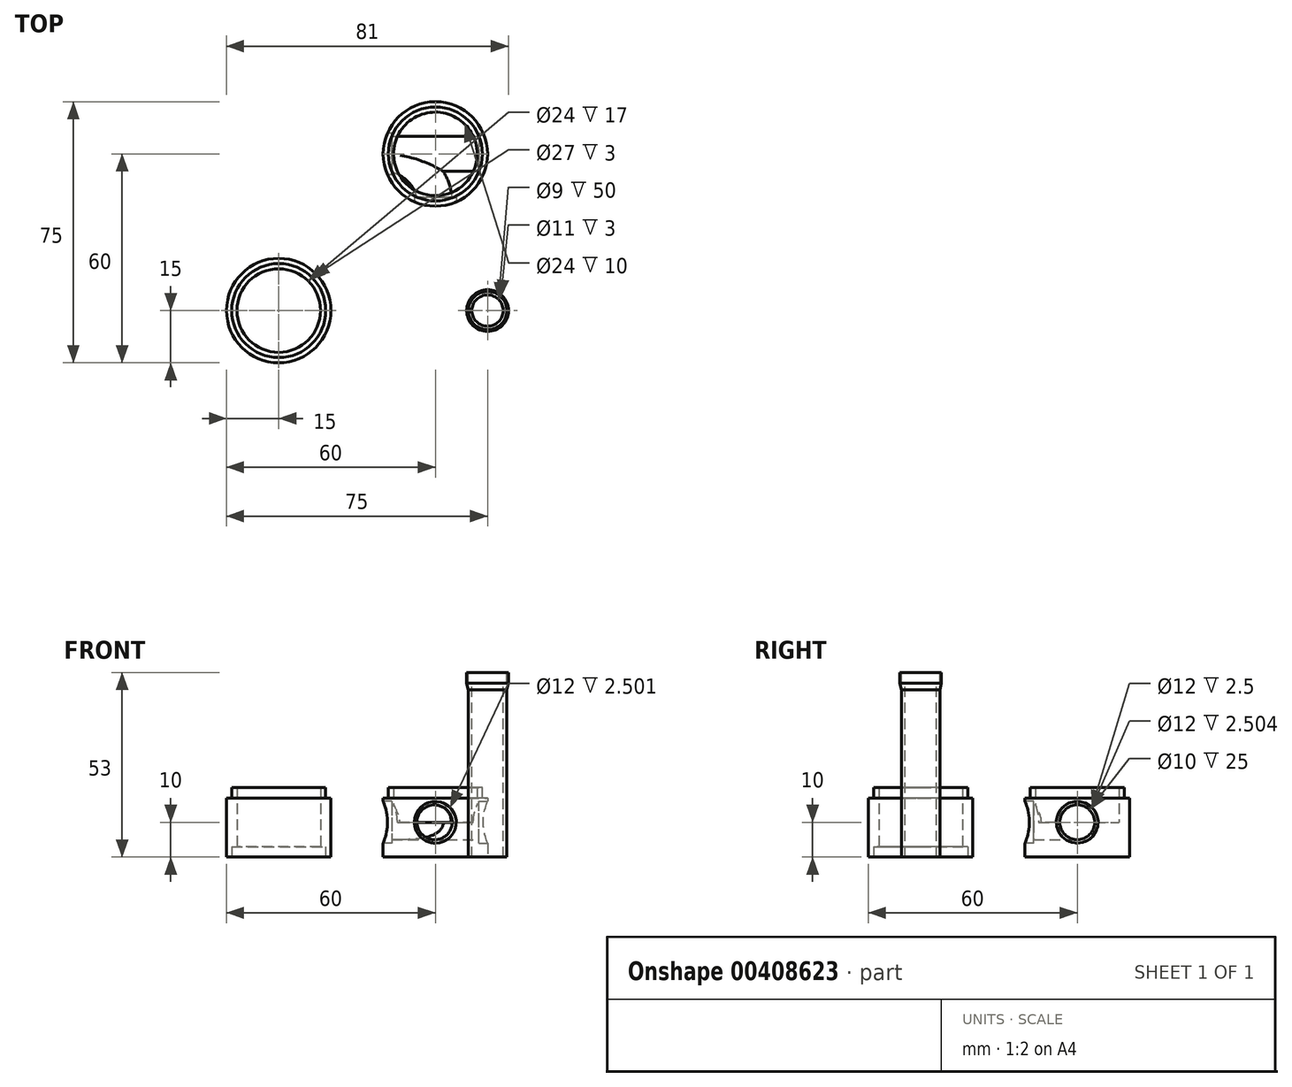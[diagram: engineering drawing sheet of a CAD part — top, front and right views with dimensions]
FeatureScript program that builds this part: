
annotation { "Feature Type Name" : "Feature", "Feature Type Description" : "" }
export const myFeature = defineFeature(function(context is Context, id is Id, definition is map)
    precondition{}
    {
        {
            var Q0;
            Q0=qCreatedBy(makeId("Top.planeOp"),FACE);
            var sketch = newSketch(context, id + "F0", { "sketchPlane" : qUnion([Q0])});
            skLineSegment(sketch, "E0.bottom", {"start": v(0, 0) * mm, "end": v(30, 0) * mm});
            skLineSegment(sketch, "E0.top", {"start": v(0, 30) * mm, "end": v(30, 30) * mm});
            skLineSegment(sketch, "E0.left", {"start": v(0, 0) * mm, "end": v(0, 30) * mm});
            skLineSegment(sketch, "E0.right", {"start": v(30, 0) * mm, "end": v(30, 30) * mm});
            skSolve(sketch);
        }
        {
            var Q0;
            Q0 = qSketchRegion(id + "F0", true);
            extrude(context, id + "F1", {"entities" : qUnion([Q0]), "depth" : 10 * mm});
        }
        {
            var Q0;
            Q0=makeQuery(id+"F1.opExtrude","CAP_FACE",FACE,{"disambiguationData":[OSD([sQuery(id+"F0.wireOp",EDGE,"E0.bottom"),sQuery(id+"F0.wireOp",EDGE,"E0.top"),sQuery(id+"F0.wireOp",EDGE,"E0.left"),sQuery(id+"F0.wireOp",EDGE,"E0.right")])],"isStart":false});
            var sketch = newSketch(context, id + "F2", { "sketchPlane" : qUnion([Q0])});
            skCircle(sketch, "E1", {"center": v(15, 15) * mm, "radius": 15 * mm});
            skPoint(sketch, "E1.centerSnap0", {"position": v(0, 15) * mm});
            skPoint(sketch, "E1.centerSnap1", {"position": v(15, 0) * mm});
            skCircle(sketch, "E2", {"center": v(15, 15) * mm, "radius": 12 * mm});
            skSolve(sketch);
        }
        {
            var Q0;
            Q0 = qSketchRegion(id + "F2", true);
            extrude(context, id + "F3", {"entities" : qUnion([Q0]), "operationType" : NewBodyOperationType.ADD, "depth" : 10 * mm});
        }
        {
            var Q0;
            Q0=makeQuery(id+"F1.opExtrude","SWEPT_FACE",FACE,{"disambiguationData":[OSD([sQuery(id+"F0.wireOp",EDGE,"E0.bottom")])]});
            var sketch = newSketch(context, id + "F4", { "sketchPlane" : qUnion([Q0])});
            skCircle(sketch, "E3", {"center": v(15, 10) * mm, "radius": 5 * mm});
            skSolve(sketch);
        }
        {
            var Q0;
            Q0=makeQuery(id+"F3.boolean.opBoolean","SPLIT",FACE,{"disambiguationData":[TD([makeQuery(id+"F3.opExtrude","SWEPT_FACE",FACE,{"disambiguationData":[OSD([sQuery(id+"F2.wireOp",EDGE,"E2")])]})])],"derivedFrom":makeQuery(id+"F1.opExtrude","CAP_FACE",FACE,{"disambiguationData":[OSD([sQuery(id+"F0.wireOp",EDGE,"E0.bottom"),sQuery(id+"F0.wireOp",EDGE,"E0.top"),sQuery(id+"F0.wireOp",EDGE,"E0.left"),sQuery(id+"F0.wireOp",EDGE,"E0.right")])],"isStart":false})});
            var sketch = newSketch(context, id + "F5", { "sketchPlane" : qUnion([Q0])});
            skArc(sketch, "E4", {"start": v(15, 0) * mm, "mid": v(10.6, 10.6) * mm, "end": v(0, 15) * mm});
            skSolve(sketch);
        }
        {
            var Q0;
            Q0 = qSketchRegion(id + "F4", true);
            var Q1;
            Q1 = qConstructionFilter(qBodyType(qCreatedBy(id + "F5" ,EDGE), BodyType.WIRE), ConstructionObject.NO);
            sweep(context, id + "F6", {"operationType" : NewBodyOperationType.REMOVE, "profiles" : qUnion([Q0]), "path" : qUnion([Q1])});
        }
        {
            var Q0;
            Q0=makeQuery(id+"F1.opExtrude","SWEPT_FACE",FACE,{"disambiguationData":[OSD([sQuery(id+"F0.wireOp",EDGE,"E0.right")])]});
            var sketch = newSketch(context, id + "F7", { "sketchPlane" : qUnion([Q0])});
            skCircle(sketch, "E5", {"center": v(15, 10) * mm, "radius": 5 * mm});
            skSolve(sketch);
        }
        {
            var Q0;
            Q0 = qSketchRegion(id + "F7", true);
            extrude(context, id + "F8", {"entities" : qUnion([Q0]), "operationType" : NewBodyOperationType.REMOVE, "oppositeDirection" : true, "depth" : 30 * mm});
        }
        {
            var Q0;
            Q0=makeQuery(id+"F1.opExtrude","SWEPT_FACE",FACE,{"disambiguationData":[OSD([sQuery(id+"F0.wireOp",EDGE,"E0.right")])]});
            var sketch = newSketch(context, id + "F9", { "sketchPlane" : qUnion([Q0])});
            skCircle(sketch, "E6", {"center": v(15, 10) * mm, "radius": 6 * mm});
            skSolve(sketch);
        }
        {
            var Q0;
            Q0 = qSketchRegion(id + "F9", true);
            extrude(context, id + "F10", {"entities" : qUnion([Q0]), "operationType" : NewBodyOperationType.REMOVE, "oppositeDirection" : true, "depth" : 2.5 * mm});
        }
        {
            var Q0;
            Q0=makeQuery(id+"F1.opExtrude","SWEPT_FACE",FACE,{"disambiguationData":[OSD([sQuery(id+"F0.wireOp",EDGE,"E0.left")])]});
            var sketch = newSketch(context, id + "F11", { "sketchPlane" : qUnion([Q0])});
            skCircle(sketch, "E7", {"center": v(-15, 10) * mm, "radius": 6 * mm});
            skSolve(sketch);
        }
        {
            var Q0;
            Q0 = qSketchRegion(id + "F11", true);
            extrude(context, id + "F12", {"entities" : qUnion([Q0]), "operationType" : NewBodyOperationType.REMOVE, "oppositeDirection" : true, "depth" : 2.5 * mm});
        }
        {
            var Q0;
            Q0=makeQuery(id+"F1.opExtrude","SWEPT_FACE",FACE,{"disambiguationData":[OSD([sQuery(id+"F0.wireOp",EDGE,"E0.bottom")])]});
            var sketch = newSketch(context, id + "F13", { "sketchPlane" : qUnion([Q0])});
            skCircle(sketch, "E8", {"center": v(15, 10) * mm, "radius": 6 * mm});
            skSolve(sketch);
        }
        {
            var Q0;
            Q0 = qSketchRegion(id + "F13", true);
            extrude(context, id + "F14", {"entities" : qUnion([Q0]), "operationType" : NewBodyOperationType.REMOVE, "oppositeDirection" : true, "depth" : 2.5 * mm});
        }
        {
            var Q0;
            Q0=makeQuery(id+"F1.opExtrude","CAP_FACE",FACE,{"disambiguationData":[OSD([sQuery(id+"F0.wireOp",EDGE,"E0.bottom"),sQuery(id+"F0.wireOp",EDGE,"E0.top"),sQuery(id+"F0.wireOp",EDGE,"E0.left"),sQuery(id+"F0.wireOp",EDGE,"E0.right")])],"isStart":true});
            var sketch = newSketch(context, id + "F15", { "sketchPlane" : qUnion([Q0])});
            skCircle(sketch, "E9", {"center": v(15, -15) * mm, "radius": 15 * mm});
            skPoint(sketch, "E9.centerSnap0", {"position": v(0, -15) * mm});
            skPoint(sketch, "E9.centerSnap1", {"position": v(15, 0) * mm});
            skSolve(sketch);
        }
        {
            var Q0;
            {var subQ0=sQuery(id+"F15.wireOp",EDGE,"E9");var subQ1=makeQuery(id+"F1.opExtrude","CAP_EDGE",EDGE,{"disambiguationData":[OSD([sQuery(id+"F0.wireOp",EDGE,"E0.bottom")])],"isStart":true});var subQ2=makeQuery(id+"F15.imprint","INTERSECT",VERTEX,{"derivedFrom":[subQ1,subQ0]});Q0=makeQuery(id+"F15.imprint","IMPRINT",FACE,{"disambiguationData":[TD([[makeQuery(id+"F15.imprint","IMPRINT",EDGE,{"disambiguationData":[TD([[subQ2,-1.0]])],"derivedFrom":subQ0}),-1.0]])]});}
            var Q1;
            {var subQ0=sQuery(id+"F15.wireOp",EDGE,"E9");var subQ1=makeQuery(id+"F1.opExtrude","CAP_EDGE",EDGE,{"disambiguationData":[OSD([sQuery(id+"F0.wireOp",EDGE,"E0.bottom")])],"isStart":true});var subQ2=makeQuery(id+"F15.imprint","INTERSECT",VERTEX,{"derivedFrom":[subQ1,subQ0]});Q1=makeQuery(id+"F15.imprint","IMPRINT",FACE,{"disambiguationData":[TD([[makeQuery(id+"F15.imprint","IMPRINT",EDGE,{"disambiguationData":[TD([[subQ2,1.0]])],"derivedFrom":subQ0}),-1.0]])]});}
            var Q2;
            {var subQ0=sQuery(id+"F15.wireOp",EDGE,"E9");var subQ1=makeQuery(id+"F1.opExtrude","CAP_EDGE",EDGE,{"disambiguationData":[OSD([sQuery(id+"F0.wireOp",EDGE,"E0.right")])],"isStart":true});var subQ2=makeQuery(id+"F15.imprint","INTERSECT",VERTEX,{"derivedFrom":[subQ1,subQ0]});Q2=makeQuery(id+"F15.imprint","IMPRINT",FACE,{"disambiguationData":[TD([[makeQuery(id+"F15.imprint","IMPRINT",EDGE,{"disambiguationData":[TD([[subQ2,1.0]])],"derivedFrom":subQ0}),-1.0]])]});}
            var Q3;
            {var subQ0=sQuery(id+"F15.wireOp",EDGE,"E9");var subQ1=makeQuery(id+"F1.opExtrude","CAP_EDGE",EDGE,{"disambiguationData":[OSD([sQuery(id+"F0.wireOp",EDGE,"E0.left")])],"isStart":true});var subQ2=makeQuery(id+"F15.imprint","INTERSECT",VERTEX,{"derivedFrom":[subQ1,subQ0]});Q3=makeQuery(id+"F15.imprint","IMPRINT",FACE,{"disambiguationData":[TD([[makeQuery(id+"F15.imprint","IMPRINT",EDGE,{"disambiguationData":[TD([[subQ2,-1.0]])],"derivedFrom":subQ0}),-1.0]])]});}
            extrude(context, id + "F16", {"entities" : qUnion([Q0, Q1, Q2, Q3]), "operationType" : NewBodyOperationType.REMOVE, "oppositeDirection" : true, "depth" : 25 * mm});
        }
        {
            var Q0;
            Q0=makeQuery(id+"F3.opExtrude","CAP_FACE",FACE,{"disambiguationData":[OSD([sQuery(id+"F2.wireOp",EDGE,"E1"),sQuery(id+"F2.wireOp",EDGE,"E2")])],"isStart":false});
            var sketch = newSketch(context, id + "F17", { "sketchPlane" : qUnion([Q0])});
            skCircle(sketch, "E10", {"center": v(15, 15) * mm, "radius": 13.5 * mm});
            skSolve(sketch);
        }
        {
            var Q0;
            Q0=makeQuery(id+"F17.imprint","IMPRINT",FACE,{"disambiguationData":[TD([[makeQuery(id+"F17.imprint","IMPRINT",EDGE,{"derivedFrom":sQuery(id+"F17.wireOp",EDGE,"E10")}),-1.0]])]});
            extrude(context, id + "F18", {"entities" : qUnion([Q0]), "operationType" : NewBodyOperationType.REMOVE, "oppositeDirection" : true, "depth" : 3 * mm});
        }
        {
            var Q0;
            Q0=qCreatedBy(makeId("Top.planeOp"),FACE);
            var sketch = newSketch(context, id + "F19", { "sketchPlane" : qUnion([Q0])});
            skLineSegment(sketch, "E11", {"start": v(0, 0) * mm, "end": v(0, -30) * mm, "construction": true});
            skLineSegment(sketch, "E12", {"start": v(0, -30) * mm, "end": v(-30, -30) * mm, "construction": true});
            skCircle(sketch, "E13", {"center": v(-30, -30) * mm, "radius": 15 * mm});
            skCircle(sketch, "E14", {"center": v(-30, -30) * mm, "radius": 12 * mm});
            skSolve(sketch);
        }
        {
            var Q0;
            Q0=makeQuery(id+"F19.imprint","IMPRINT",FACE,{"disambiguationData":[TD([[makeQuery(id+"F19.imprint","IMPRINT",EDGE,{"derivedFrom":sQuery(id+"F19.wireOp",EDGE,"E13")}),1.0]])]});
            extrude(context, id + "F20", {"entities" : qUnion([Q0]), "depth" : 20 * mm});
        }
        {
            var Q0;
            Q0=makeQuery(id+"F20.opExtrude","CAP_FACE",FACE,{"disambiguationData":[OSD([sQuery(id+"F19.wireOp",EDGE,"E13"),sQuery(id+"F19.wireOp",EDGE,"E14")])],"isStart":true});
            var sketch = newSketch(context, id + "F21", { "sketchPlane" : qUnion([Q0])});
            skCircle(sketch, "E15", {"center": v(-30, 30) * mm, "radius": 13.5 * mm});
            skSolve(sketch);
        }
        {
            var Q0;
            Q0=makeQuery(id+"F21.imprint","IMPRINT",FACE,{"disambiguationData":[TD([[makeQuery(id+"F21.imprint","IMPRINT",EDGE,{"derivedFrom":sQuery(id+"F21.wireOp",EDGE,"E15")}),1.0]])]});
            extrude(context, id + "F22", {"entities" : qUnion([Q0]), "operationType" : NewBodyOperationType.REMOVE, "oppositeDirection" : true, "depth" : 3 * mm});
        }
        {
            var Q0;
            Q0=makeQuery(id+"F20.opExtrude","CAP_FACE",FACE,{"disambiguationData":[OSD([sQuery(id+"F19.wireOp",EDGE,"E13"),sQuery(id+"F19.wireOp",EDGE,"E14")])],"isStart":false});
            var sketch = newSketch(context, id + "F23", { "sketchPlane" : qUnion([Q0])});
            skCircle(sketch, "E16", {"center": v(-30, -30) * mm, "radius": 13.5 * mm});
            skSolve(sketch);
        }
        {
            var Q0;
            Q0=makeQuery(id+"F23.imprint","IMPRINT",FACE,{"disambiguationData":[TD([[makeQuery(id+"F23.imprint","IMPRINT",EDGE,{"derivedFrom":sQuery(id+"F23.wireOp",EDGE,"E16")}),-1.0]])]});
            extrude(context, id + "F24", {"entities" : qUnion([Q0]), "operationType" : NewBodyOperationType.REMOVE, "oppositeDirection" : true, "depth" : 3 * mm});
        }
        {
            var Q0;
            Q0=qCreatedBy(makeId("Top.planeOp"),FACE);
            var sketch = newSketch(context, id + "F25", { "sketchPlane" : qUnion([Q0])});
            skLineSegment(sketch, "E17", {"start": v(0, 0) * mm, "end": v(0, -30) * mm, "construction": true});
            skLineSegment(sketch, "E18", {"start": v(0, -30) * mm, "end": v(30, -30) * mm, "construction": true});
            skCircle(sketch, "E19", {"center": v(30, -30) * mm, "radius": 5.5 * mm});
            skSolve(sketch);
        }
        {
            var Q0;
            Q0 = qSketchRegion(id + "F25", true);
            extrude(context, id + "F26", {"entities" : qUnion([Q0]), "depth" : 50 * mm});
        }
        {
            var Q0;
            Q0=makeQuery(id+"F26.opExtrude","CAP_FACE",FACE,{"disambiguationData":[OSD([sQuery(id+"F25.wireOp",EDGE,"E19")])],"isStart":false});
            var sketch = newSketch(context, id + "F27", { "sketchPlane" : qUnion([Q0])});
            skCircle(sketch, "E20", {"center": v(30, -30) * mm, "radius": 4.5 * mm});
            skSolve(sketch);
        }
        {
            var Q0;
            Q0=makeQuery(id+"F27.imprint","IMPRINT",FACE,{"disambiguationData":[TD([[makeQuery(id+"F27.imprint","IMPRINT",EDGE,{"derivedFrom":sQuery(id+"F27.wireOp",EDGE,"E20")}),1.0]])]});
            extrude(context, id + "F28", {"entities" : qUnion([Q0]), "operationType" : NewBodyOperationType.REMOVE, "oppositeDirection" : true, "depth" : 50 * mm});
        }
        {
            var Q0;
            Q0=makeQuery(id+"F26.opExtrude","CAP_FACE",FACE,{"disambiguationData":[OSD([sQuery(id+"F25.wireOp",EDGE,"E19")])],"isStart":false});
            var sketch = newSketch(context, id + "F29", { "sketchPlane" : qUnion([Q0])});
            skCircle(sketch, "E21", {"center": v(30, -30) * mm, "radius": 6 * mm});
            skCircle(sketch, "E22", {"center": v(30, -30) * mm, "radius": 5.5 * mm});
            skSolve(sketch);
        }
        {
            var Q0;
            Q0=makeQuery(id+"F29.imprint","IMPRINT",FACE,{"disambiguationData":[TD([[makeQuery(id+"F29.imprint","IMPRINT",EDGE,{"derivedFrom":sQuery(id+"F29.wireOp",EDGE,"E21")}),1.0]])]});
            extrude(context, id + "F30", {"entities" : qUnion([Q0]), "operationType" : NewBodyOperationType.ADD, "oppositeDirection" : true, "depth" : 2 * mm, "hasSecondDirection" : true, "secondDirectionOppositeDirection" : false, "secondDirectionDepth" : 3 * mm});
        }
        {
            var Q0;
            Q0=makeQuery(id+"F30.opExtrude","CAP_EDGE",EDGE,{"disambiguationData":[OSD([sQuery(id+"F29.wireOp",EDGE,"E21")])],"isStart":false});
            chamfer(context, id + "F31", {"entities" : qUnion([Q0]), "chamferType" : ChamferType.TWO_OFFSETS, "width1" : 2 * mm, "oppositeDirection" : false, "width2" : 0.5 * mm, "tangentPropagation" : true});
        }
    });
